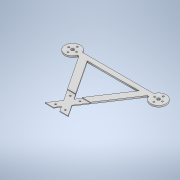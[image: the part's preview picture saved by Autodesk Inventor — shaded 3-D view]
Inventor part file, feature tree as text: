
AUTODESK INVENTOR PART (.ipt)
format: ipt  version: 2020 (Build 240168000, 168)  size: 285,184 bytes
history: native  units: in
note: dims shown in document units (in); Inventor stores cm internally (conversion verified against a paired STEP export)
features: extrude x4, sketch x4, plane x1, mirror x1
ambient origin geometry x8: Origin, YZ Plane, XZ Plane, XY Plane, X Axis, Y Axis, Z Axis, Center Point
bodies: Solid1 (feature_tree)
feature tree (10):
  extrude  "Extrusion1"  Depth=0.125in
  plane  "Work Plane1"
  mirror  "Mirror1"
  extrude  "Extrusion2"  Depth=0.125in
  extrude  "Extrusion3"  Depth=0.378in
  extrude  "Extrusion4"  Depth=0.319in
  sketch  "Sketch1"  dims[d0=0.25in d1=0.125in]
  sketch  "Sketch2"  dims[d2=0.125in d3=0.125in]
  sketch  "Sketch3"  dims[d4=0.125in d5=0.378in]
  sketch  "Sketch4"  dims[d6=0.319in d7=0.319in d8=0.378in d9=1.25in d10=0.12in d11=0.0in d14=0.2in d15=0.2in d16=0.2in d17=0.2in d18=3.675in d26=0.12in d27=0.0in d33=0.06in d34=0.0in d45=0.15in d46=0.0in d50=6.957in d58=0.898in d64=0.898in d65=0.898in d67=0.9041in d69=0.927in d70=0.927in d74=0.125in d75=0.125in d76=0.125in d77=0.125in d78=0.2306in d79=0.2306in d81=90.0deg d82=0.898in d83=0.898in]
